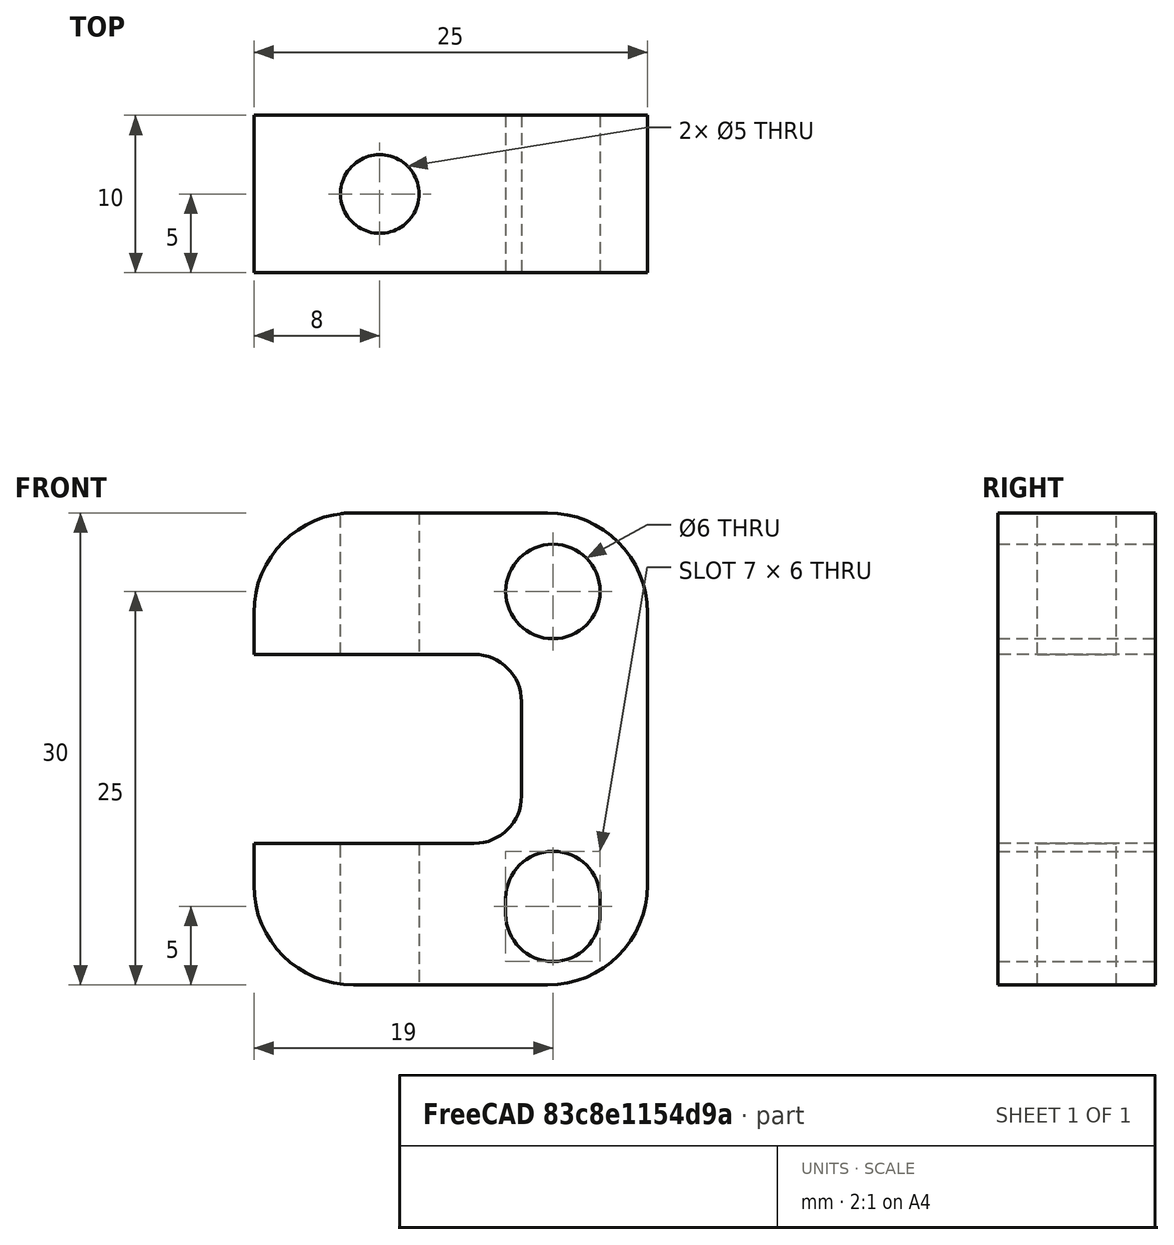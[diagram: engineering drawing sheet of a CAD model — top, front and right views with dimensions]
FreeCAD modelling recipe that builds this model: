
FCSTD DOCUMENT  (FreeCAD 0.19R23578 (Git))
Label: y_idler_holder
License: All rights reserved
LicenseURL: http://en.wikipedia.org/wiki/All_rights_reserved
objects: TechDraw::DrawViewDimension×12, TechDraw::DrawProjGroupItem×4, Sketcher::SketchObject×2, TechDraw::DrawProjGroup×2, TechDraw::DrawViewDimExtent×2, PartDesign::CoordinateSystem×2, PartDesign::Pad×1, PartDesign::Pocket×1, PartDesign::Body×1, TechDraw::DrawSVGTemplate×1, TechDraw::DrawPage×1, App::Part×1
note: 9 computed .brp shape members not serialized (recipe doc carries the construction recipe); baked Part::Feature solids carry a one-line shape summary decoded from their .brp

FEATURE [Sketcher::SketchObject] Sketch091
  MapMode = 5
  Placement = pos=(0,0,0) rot=(1,0,0;1.5708rad)
  Support = -> [XZ_Plane104]
  sketch-geometry (22):
    g0: LineSegment StartX=-2.65 StartY=15 StartZ=0 EndX=9.65 EndY=15 EndZ=0
    g1: LineSegment StartX=16 StartY=8.65 StartZ=0 EndX=16 EndY=-8.65 EndZ=0
    g2: LineSegment StartX=9.65 StartY=-15 StartZ=0 EndX=-2.65 EndY=-15 EndZ=0
    g3: LineSegment StartX=-9 StartY=-8.65 StartZ=0 EndX=-9 EndY=-6 EndZ=0
    g4: ArcOfCircle CenterX=9.65 CenterY=8.65 CenterZ=0 NormalX=0 NormalY=0 NormalZ=1 AngleXU=0 Radius=6.35 StartAngle=0 EndAngle=1.5708
    g5: ArcOfCircle CenterX=-2.65 CenterY=8.65 CenterZ=0 NormalX=0 NormalY=0 NormalZ=1 AngleXU=0 Radius=6.35 StartAngle=1.5708 EndAngle=3.14159
    g6: ArcOfCircle CenterX=-2.65 CenterY=-8.65 CenterZ=0 NormalX=0 NormalY=0 NormalZ=1 AngleXU=0 Radius=6.35 StartAngle=3.14159 EndAngle=4.71239
    g7: ArcOfCircle CenterX=9.65 CenterY=-8.65 CenterZ=0 NormalX=0 NormalY=0 NormalZ=1 AngleXU=0 Radius=6.35 StartAngle=4.71239 EndAngle=6.28319
    g8: Circle CenterX=10 CenterY=10 CenterZ=0 NormalX=0 NormalY=0 NormalZ=1 AngleXU=0 Radius=3
    g9: ArcOfCircle CenterX=10 CenterY=-9.5 CenterZ=0 NormalX=0 NormalY=0 NormalZ=1 AngleXU=0 Radius=3 StartAngle=2e-16 EndAngle=3.14159
    g10: ArcOfCircle CenterX=10 CenterY=-10.5 CenterZ=0 NormalX=0 NormalY=0 NormalZ=1 AngleXU=0 Radius=3 StartAngle=3.14159 EndAngle=6.28319
    g11: LineSegment StartX=7 StartY=-9.5 StartZ=0 EndX=7 EndY=-10.5 EndZ=0
    g12: LineSegment StartX=13 StartY=-9.5 StartZ=0 EndX=13 EndY=-10.5 EndZ=0
    g13: GeomPoint X=10 Y=-10 Z=0
    g14: LineSegment StartX=10 StartY=-9.5 StartZ=0 EndX=10 EndY=-10 EndZ=0
    g15: LineSegment StartX=10 StartY=-10 StartZ=0 EndX=10 EndY=-10.5 EndZ=0
    g16: LineSegment StartX=-9 StartY=6 StartZ=0 EndX=-9 EndY=8.65 EndZ=0
    g17: LineSegment StartX=-9 StartY=6 StartZ=0 EndX=5 EndY=6 EndZ=0
    g18: LineSegment StartX=8 StartY=3 StartZ=0 EndX=8 EndY=-3 EndZ=0
    g19: LineSegment StartX=5 StartY=-6 StartZ=0 EndX=-9 EndY=-6 EndZ=0
    g20: ArcOfCircle CenterX=5 CenterY=3 CenterZ=0 NormalX=0 NormalY=0 NormalZ=1 AngleXU=0 Radius=3 StartAngle=0 EndAngle=1.5708
    g21: ArcOfCircle CenterX=5 CenterY=-3 CenterZ=0 NormalX=0 NormalY=0 NormalZ=1 AngleXU=0 Radius=3 StartAngle=4.71239 EndAngle=6.28319
  constraints (51):
    c: Horizontal(g0)
    c: Horizontal(g2)
    c: Vertical(g1)
    c: Tangent(g0,g4) = 1.5708
    c: Tangent(g1,g4) = 1.5708
    c: Tangent(g0,g5) = 1.5708
    c: Tangent(g2,g6) = 1.5708
    c: Tangent(g3,g6) = 1.5708
    c: Tangent(g1,g7) = 1.5708
    c: Tangent(g2,g7) = 1.5708
    c: Equal(g4,g5)
    c: Equal(g5,g6)
    c: Symmetric(g2,g0,g-1)
    c: DistanceY(g2,g0) = 30
    c: DistanceX(g-1,g1) = 16
    c: Radius(g4) = 6.35
    c: DistanceX(g16,g-1) = 9
    c: Tangent(g9,g12)
    c: Tangent(g9,g11)
    c: Tangent(g11,g10)
    c: Tangent(g12,g10)
    c: Vertical(g11)
    c: Equal(g9,g10)
    c: Equal(g9,g8)
    c: Diameter(g8) = 6
    c: DistanceY(g12,g12) = 1
    c: Vertical(g9,g8)
    c: DistanceX(g-1,g8) = 10
    c: Coincident(g14,g9)
    c: Coincident(g14,g13)
    c: Coincident(g15,g13)
    c: Coincident(g15,g10)
    c: Equal(g15,g14)
    c: Symmetric(g13,g8,g-1)
    c: DistanceY(g-1,g8) = 10
    c: Tangent(g3,g16)
    c: Coincident(g16,g17)
    c: Horizontal(g17)
    c: Coincident(g19,g3)
    c: Horizontal(g19)
    c: Tangent(g17,g20) = 1.5708
    c: Tangent(g18,g20) = 1.5708
    c: Tangent(g18,g21) = 1.5708
    c: Tangent(g19,g21) = 1.5708
    c: Equal(g21,g20)
    c: Radius(g20) = 3
    c: Vertical(g18)
    c: Symmetric(g3,g16,g-1)
    c: DistanceX(g-1,g18) = 8
    c: DistanceY(g3,g16) = 12
    c: Tangent(g16,g5) = 1.5708
FEATURE [PartDesign::Pad] Pad031  label="Pad032"
  Direction = (1,1,1)
  Length = 10
  Length2 = 100
  Placement = pos=(0,0,0) rot=(1,0,0;1.5708rad)
  Profile = -> Sketch091
  Type = 0
FEATURE [Sketcher::SketchObject] Sketch092
  MapMode = 5
  Support = -> [XY_Plane104]
  expr: Constraints[0] = Pad031.Length / 2
  sketch-geometry (1):
    g0: Circle CenterX=-1 CenterY=-5 CenterZ=0 NormalX=0 NormalY=0 NormalZ=1 AngleXU=0 Radius=2.5
  constraints (3):
    c: DistanceY(g0,g-1) = 5
    c: Diameter(g0) = 5
    c: DistanceX(g0,g-1) = 1
FEATURE [PartDesign::Pocket] Pocket026
  BaseFeature = -> Pad031
  Length = 5
  Length2 = 100
  Midplane = true
  Placement = pos=(0,0,0) rot=(1,0,0;1.5708rad)
  Profile = -> Sketch092
  Type = 1
FEATURE [PartDesign::Body] Body035  label="Body"
  Group = -> [Sketch091,Pad031,Sketch092,Pocket026]
  Origin = -> Origin104
  Tip = -> Pocket026
FEATURE [TechDraw::DrawSVGTemplate] Template009
  EditableTexts = Author=Alex neufeld; DWG_num=2020-010; Date=08/07/2020; Revision=1; Scale=NTS; Subtitle=1 Req.; Title=Y Axis Idler holder
  Height = 215.9
  Orientation = 1
  Width = 279.4
FEATURE [TechDraw::DrawProjGroupItem] ProjItem032  label="Front009"
  CoarseView = false
  Direction = (0.577,-0.577,0.577)
  Focus = 100
  HardHidden = false
  IsoCount = 0
  IsoHidden = false
  IsoVisible = false
  LockPosition = true
  Perspective = false
  Rotation = 0
  RotationVector = (0.707,0.707,0)
  ScaleType = 2
  SeamHidden = false
  SeamVisible = true
  SmoothHidden = false
  SmoothVisible = true
  Source = -> [Body035]
  Type = 0
  X = 0
  XDirection = (0.707,0.707,0)
  Y = 0
FEATURE [TechDraw::DrawProjGroup] ProjGroup009
  Anchor = -> ProjItem032
  AutoDistribute = true
  LockPosition = false
  ProjectionType = 0
  Rotation = 0
  ScaleType = 0
  Source = -> [Body035]
  Views = -> [ProjItem032]
  X = 33.3834
  Y = 182.193
  spacingX = 15
  spacingY = 15
FEATURE [TechDraw::DrawProjGroupItem] ProjItem033  label="Front010"
  CoarseView = false
  Direction = (0,1,0)
  Focus = 100
  HardHidden = false
  IsoCount = 0
  IsoHidden = false
  IsoVisible = false
  LockPosition = true
  Perspective = false
  Rotation = 0
  RotationVector = (-1,0,0)
  Scale = 2
  ScaleType = 2
  SeamHidden = false
  SeamVisible = true
  SmoothHidden = false
  SmoothVisible = true
  Source = -> [Body035]
  Type = 0
  X = 0
  XDirection = (-1,0,0)
  Y = 0
FEATURE [TechDraw::DrawProjGroupItem] ProjItem034  label="Bottom007"
  CoarseView = false
  Direction = (0,0,-1)
  Focus = 100
  HardHidden = false
  IsoCount = 0
  IsoHidden = false
  IsoVisible = false
  LockPosition = false
  Perspective = false
  Rotation = 0
  RotationVector = (1,0,0)
  Scale = 2
  ScaleType = 2
  SeamHidden = false
  SeamVisible = true
  SmoothHidden = false
  SmoothVisible = true
  Source = -> [Body035]
  Type = 5
  X = 0
  XDirection = (-1,0,0)
  Y = 55
FEATURE [TechDraw::DrawProjGroupItem] ProjItem035  label="Left005"
  CoarseView = false
  Direction = (1,1e-16,0)
  Focus = 100
  HardHidden = false
  IsoCount = 0
  IsoHidden = false
  IsoVisible = false
  LockPosition = false
  Perspective = false
  Rotation = 0
  RotationVector = (1,0,0)
  Scale = 2
  ScaleType = 2
  SeamHidden = false
  SeamVisible = true
  SmoothHidden = false
  SmoothVisible = true
  Source = -> [Body035]
  Type = 1
  X = 50
  XDirection = (-1e-16,1,0)
  Y = 0
FEATURE [TechDraw::DrawProjGroup] ProjGroup010
  Anchor = -> ProjItem033
  AutoDistribute = true
  LockPosition = false
  ProjectionType = 0
  Rotation = 0
  Scale = 2
  ScaleType = 2
  Source = -> [Body035]
  Views = -> [ProjItem033,ProjItem034,ProjItem035]
  X = 120.1
  Y = 98.1499
  spacingX = 15
  spacingY = 15
FEATURE [TechDraw::DrawViewDimension] Dimension167
  Arbitrary = false
  ArbitraryTolerances = false
  FormatSpec = %.3f
  FormatSpecOverTolerance = %+.2f
  FormatSpecUnderTolerance = %+.2f
  Inverted = false
  LockPosition = false
  MeasureType = 1
  OverTolerance = 0
  References2D = -> [ProjItem034]
  Rotation = 0
  ScaleType = 0
  TheoreticalExact = false
  Type = 1
  UnderTolerance = 0
  X = -9.04591
  Y = 16.4411
FEATURE [TechDraw::DrawViewDimension] Dimension168
  Arbitrary = false
  ArbitraryTolerances = false
  FormatSpec = %.3f
  FormatSpecOverTolerance = %+.2f
  FormatSpecUnderTolerance = %+.2f
  Inverted = false
  LockPosition = false
  MeasureType = 1
  OverTolerance = 0
  References2D = -> [ProjItem034]
  Rotation = 0
  ScaleType = 0
  TheoreticalExact = false
  Type = 2
  UnderTolerance = 0
  X = 28.9989
  Y = -3.3004
FEATURE [TechDraw::DrawViewDimension] Dimension169
  Arbitrary = false
  ArbitraryTolerances = false
  FormatSpec = %.3f
  FormatSpecOverTolerance = %+.2f
  FormatSpecUnderTolerance = %+.2f
  Inverted = false
  LockPosition = false
  MeasureType = 1
  OverTolerance = 0
  References2D = -> [ProjItem033]
  Rotation = 0
  ScaleType = 0
  TheoreticalExact = false
  Type = 1
  UnderTolerance = 0
  X = -3.02004
  Y = -43.9785
FEATURE [TechDraw::DrawViewDimension] Dimension170
  Arbitrary = false
  ArbitraryTolerances = false
  FormatSpec = %.3f
  FormatSpecOverTolerance = %+.2f
  FormatSpecUnderTolerance = %+.2f
  Inverted = false
  LockPosition = false
  MeasureType = 1
  OverTolerance = 0
  References2D = -> [ProjItem033]
  Rotation = 0
  ScaleType = 0
  TheoreticalExact = false
  Type = 2
  UnderTolerance = 0
  X = -43.5614
  Y = -21.914
FEATURE [TechDraw::DrawViewDimension] Dimension171
  Arbitrary = false
  ArbitraryTolerances = false
  FormatSpec = %.3f
  FormatSpecOverTolerance = %+.2f
  FormatSpecUnderTolerance = %+.2f
  Inverted = false
  LockPosition = false
  MeasureType = 1
  OverTolerance = 0
  References2D = -> [ProjItem033]
  Rotation = 0
  ScaleType = 0
  TheoreticalExact = false
  Type = 2
  UnderTolerance = 0
  X = 25
  Y = -3.6e-15
FEATURE [TechDraw::DrawViewDimension] Dimension172
  Arbitrary = false
  ArbitraryTolerances = false
  FormatSpec = R%.3f
  FormatSpecOverTolerance = %+.2f
  FormatSpecUnderTolerance = %+.2f
  Inverted = false
  LockPosition = false
  MeasureType = 1
  OverTolerance = 0
  References2D = -> [ProjItem033]
  Rotation = 0
  ScaleType = 0
  TheoreticalExact = false
  Type = 4
  UnderTolerance = 0
  X = -0.941315
  Y = -1.31784
FEATURE [TechDraw::DrawViewDimension] Dimension173
  Arbitrary = false
  ArbitraryTolerances = false
  FormatSpec = ⌀%.3f
  FormatSpecOverTolerance = %+.2f
  FormatSpecUnderTolerance = %+.2f
  Inverted = false
  LockPosition = false
  MeasureType = 1
  OverTolerance = 0
  References2D = -> [ProjItem033]
  Rotation = 0
  ScaleType = 0
  TheoreticalExact = false
  Type = 5
  UnderTolerance = 0
  X = -32.5695
  Y = 38.0291
FEATURE [TechDraw::DrawViewDimExtent] DimExtent011
  Arbitrary = false
  ArbitraryTolerances = false
  CosmeticTags = 4f44505d-5166-429b-bd56-ebb3d7bf540a | 42bec0fc-47a3-41a0-9c52-be35370a75bc
  DirExtent = 1
  FormatSpec = %.3f
  FormatSpecOverTolerance = %+.2f
  FormatSpecUnderTolerance = %+.2f
  Inverted = false
  LockPosition = false
  MeasureType = 1
  OverTolerance = 0
  References2D = -> [ProjItem035]
  Rotation = 0
  ScaleType = 0
  Source = -> [ProjItem035]
  TheoreticalExact = false
  Type = 2
  UnderTolerance = 0
  X = 14.308
  Y = 0.564789
FEATURE [TechDraw::DrawViewDimExtent] DimExtent012
  Arbitrary = false
  ArbitraryTolerances = false
  CosmeticTags = 225fc8d8-6159-4144-9f91-1bdc64712757 | b8afe412-8ad3-4052-9b81-7dccc0b6091b
  DirExtent = 0
  FormatSpec = %.3f
  FormatSpecOverTolerance = %+.2f
  FormatSpecUnderTolerance = %+.2f
  Inverted = false
  LockPosition = false
  MeasureType = 1
  OverTolerance = 0
  References2D = -> [ProjItem035]
  Rotation = 0
  ScaleType = 0
  Source = -> [ProjItem035]
  TheoreticalExact = false
  Type = 1
  UnderTolerance = 0
  X = 2.82395
  Y = 44.6183
FEATURE [TechDraw::DrawViewDimension] Dimension174
  Arbitrary = false
  ArbitraryTolerances = false
  FormatSpec = %.3f
  FormatSpecOverTolerance = %+.2f
  FormatSpecUnderTolerance = %+.2f
  Inverted = false
  LockPosition = false
  MeasureType = 1
  OverTolerance = 0
  References2D = -> [ProjItem033]
  Rotation = 0
  ScaleType = 0
  TheoreticalExact = false
  Type = 2
  UnderTolerance = 0
  X = -35.9053
  Y = 0.470657
FEATURE [TechDraw::DrawViewDimension] Dimension175
  Arbitrary = false
  ArbitraryTolerances = false
  FormatSpec = R%.3f
  FormatSpecOverTolerance = %+.2f
  FormatSpecUnderTolerance = %+.2f
  Inverted = false
  LockPosition = false
  MeasureType = 1
  OverTolerance = 0
  References2D = -> [ProjItem033]
  Rotation = 0
  ScaleType = 0
  TheoreticalExact = false
  Type = 4
  UnderTolerance = 0
  X = 21.3365
  Y = 38.1233
FEATURE [TechDraw::DrawViewDimension] Dimension176
  Arbitrary = false
  ArbitraryTolerances = false
  FormatSpec = ⌀%.3f
  FormatSpecOverTolerance = %+.2f
  FormatSpecUnderTolerance = %+.2f
  Inverted = false
  LockPosition = false
  MeasureType = 1
  OverTolerance = 0
  References2D = -> [ProjItem034]
  Rotation = 0
  ScaleType = 0
  TheoreticalExact = false
  Type = 5
  UnderTolerance = 0
  X = -14.8487
  Y = -24.2529
FEATURE [TechDraw::DrawViewDimension] Dimension177
  Arbitrary = false
  ArbitraryTolerances = false
  FormatSpec = %.3f
  FormatSpecOverTolerance = %+.2f
  FormatSpecUnderTolerance = %+.2f
  Inverted = false
  LockPosition = false
  MeasureType = 1
  OverTolerance = 0
  References2D = -> [ProjItem033]
  Rotation = 0
  ScaleType = 0
  TheoreticalExact = false
  Type = 1
  UnderTolerance = 0
  X = 8
  Y = 9
FEATURE [TechDraw::DrawViewDimension] Dimension178
  Arbitrary = false
  ArbitraryTolerances = false
  FormatSpec = %.3f
  FormatSpecOverTolerance = %+.2f
  FormatSpecUnderTolerance = %+.2f
  Inverted = false
  LockPosition = false
  MeasureType = 1
  OverTolerance = 0
  References2D = -> [ProjItem033]
  Rotation = 0
  ScaleType = 0
  TheoreticalExact = false
  Type = 1
  UnderTolerance = 0
  X = -20.9798
  Y = -36.221
FEATURE [TechDraw::DrawPage] Page009  label="y_tensioner"
  KeepUpdated = false
  NextBalloonIndex = 1
  ProjectionType = 0
  Template = -> Template009
  Views = -> [ProjGroup009,ProjGroup010,Dimension167,Dimension168,Dimension169,Dimension170,Dimension171,Dimension172,Dimension173,DimExtent011,DimExtent012,Dimension174,Dimension175,Dimension176,Dimension177,Dimension178]
FEATURE [PartDesign::CoordinateSystem] LCS_1
  AttacherType = Attacher::AttachEngine3D
  MapMode = 11
  Placement = pos=(10,-10,10) rot=(0.57735,-0.57735,0.57735;2.0944rad)
  Support = -> [Pocket026]
FEATURE [PartDesign::CoordinateSystem] LCS_2
  AttacherType = Attacher::AttachEngine3D
  MapMode = 45
  Placement = pos=(-1,-5,0) rot=(0.57735,0.57735,0.57735;2.0944rad)
  Support = -> [Pocket026]
FEATURE [App::Part] Part  label="y_idler_holder"
  Group = -> [Body035,LCS_1,LCS_2]
  Origin = -> Origin
